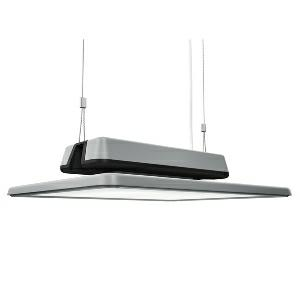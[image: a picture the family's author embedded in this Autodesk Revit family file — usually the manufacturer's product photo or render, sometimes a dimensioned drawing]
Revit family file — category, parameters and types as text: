
# Revit family: acaneo_-_hial_20000_840_w_ea_00734332_8f37
name_source: partatom
category: Lighting Fixtures
units: mm (PartAtom-declared; Revit-internal decimal feet)

## family parameters
Cut with Voids When Loaded = No
Host = Face
Light Source = No
Part Type = Normal
Room Calculation Point = No
Round Connector Dimension = Use Diameter
Shared = No

## types (1)
- ACANEO - HIAL 20000/840/W/EA (1 x LED, 22000 lm, 4000K)
    Apparent Load = 140 VA
    Approval mark = CE
    CIE Flux Codes = 76 97 99 100 100
    Color Rendering = 80-89
    Color Temperature = 4000K
    Control Gear = Electronic ballast
    Default Elevation = 1800 mm
    Description = HIAL 20000/840/W/EA|High bay luminaire|light source: LED|work equipment: Electronic ballast|connected load: 220-240 V, 50/60 Hz|Power consumption: approx. 140 W|power factor: approx. 0,951|luminous flux: 22000 lm|luminous efficacy: 157 lm/W|colour temperature: Cold white, ca. 4000 K|color rendering index (CRI): >= 80|chromaticity tolerance:  3 SDCM|System of protection: IP 65|class of protection: I|technology: Switchable|luminaire body|material: Aluminium|surface: Powder coatet|colour: White aluminium|lamp cover: Acrylic (PMMA), Clear|weight (net): approx. 8.2 kg|mains lead: Built-in plug RST 25i3 Einbau|Fastening: Available separately|Accessory: Junction box (RST 2013)|minimum ambient temperature: -30 ░C|maximum ambient temperature: 50 ░C|glare control: Optics|unified glare rating(4H 8H): <=  25|
    Frequency = 50 Hz, 60 Hz
    Height = 125 mm
    Lamp = 1 x LED
    Lamp Light Flux = 22000 lm
    Lamp count = 1
    Length = 480 mm
    Luminous efficacy = 157 lm/W
    Manufacturer = Waldmann
    ModVariant = No
    Model = 00734332
    Mounting Place = Ceiling
    Mounting Type = Pendant
    Number of Poles = 1
    OnlyDefault = Yes
    Power Factor = 1
    Product Name = ACANEO - HIAL 20000/840/W/EA
    Product group = High bay luminaire (industry)
    ProductGroupID = 901
    Protection Class = Protection class I
    Protection Degree = IP 65
    RLX_Detail_Level = 1
    RLX_Emergency_Light_Flux = 0 lm
    RLX_Emergency_Type = 0
    RLX_Emergency_Type_DB = No
    RlxData = <blob elided: 31213 chars, md5=da76b38a>
    Socket = socket
    Standby Power = 0 W
    System Light Flux = 22000 lm
    System Power = 140 W
    Type Comments = Product without accessories
    Type Image = acaneo-hial.jpg
    URL = http://relux.com
    VarID = ---
    Voltage = 230 V
    Voltage Range = 110-120 V, 220-240 V
    Weight = 0.00 kg
    Width = 405 mm

## geometry (parser evidence)
native form markers: Blend x4, Sweep x8
no freeform markers — native parametric forms only
